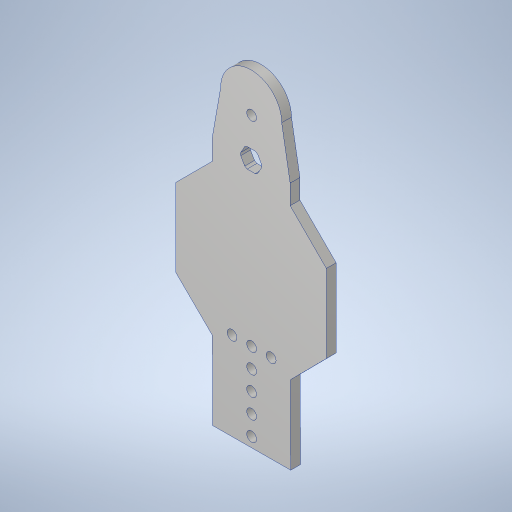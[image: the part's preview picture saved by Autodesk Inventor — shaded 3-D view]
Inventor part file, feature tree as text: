
AUTODESK INVENTOR PART (.ipt)
format: ipt  version: 2023.4 (Build 274418000, 418)  size: 315,904 bytes
history: native  units: in
note: dims shown in document units (in); Inventor stores cm internally (conversion verified against a paired STEP export)
features: extrude x2, sketch x2, hole x1
ambient origin geometry x8: Origin, YZ Plane, XZ Plane, XY Plane, X Axis, Y Axis, Z Axis, Center Point
bodies: Solid1 (feature_tree)
feature tree (5):
  extrude  "Extrusion1"  Depth=2.0in
  sketch  "Sketch2"  dims[d2=1.311in d3=1.311in d4=135.0deg d5=135.0deg d6=2.0in d7=2.0in d8=1.311in d9=1.311in d10=135.0deg d11=135.0deg d12=0.5in d13=0.5in d15=1.25in d16=1.1681in d17=1.25in d18=1.1681in d19=0.25in d20=0.0in d21=0.25in d22=1.0in d23=0.5in d24=0.5in d25=0.5in d26=0.5in d27=0.5in d28=0.5in d29=1.0in d31=1.0in d32=0.25in d33=0.75in d34=0.507in d35=0.25in d36=0.5635in d37=1.0in d38=0.8108in d39=0.25in d40=0.0in d41=0.541in d42=0.5in]
  hole  "Hole1"  [1 undecoded]
  extrude  "Extrusion2"  TaperAngle=135.0deg  [1 undecoded]
  sketch  "Sketch1"  dims[d0=2.0in d1=2.0in]
note: 2 required parameter values undecoded (feature->parameter linkage not recoverable at this tier; creation-order binding heuristic only, values carry confidence <= 0.55)
